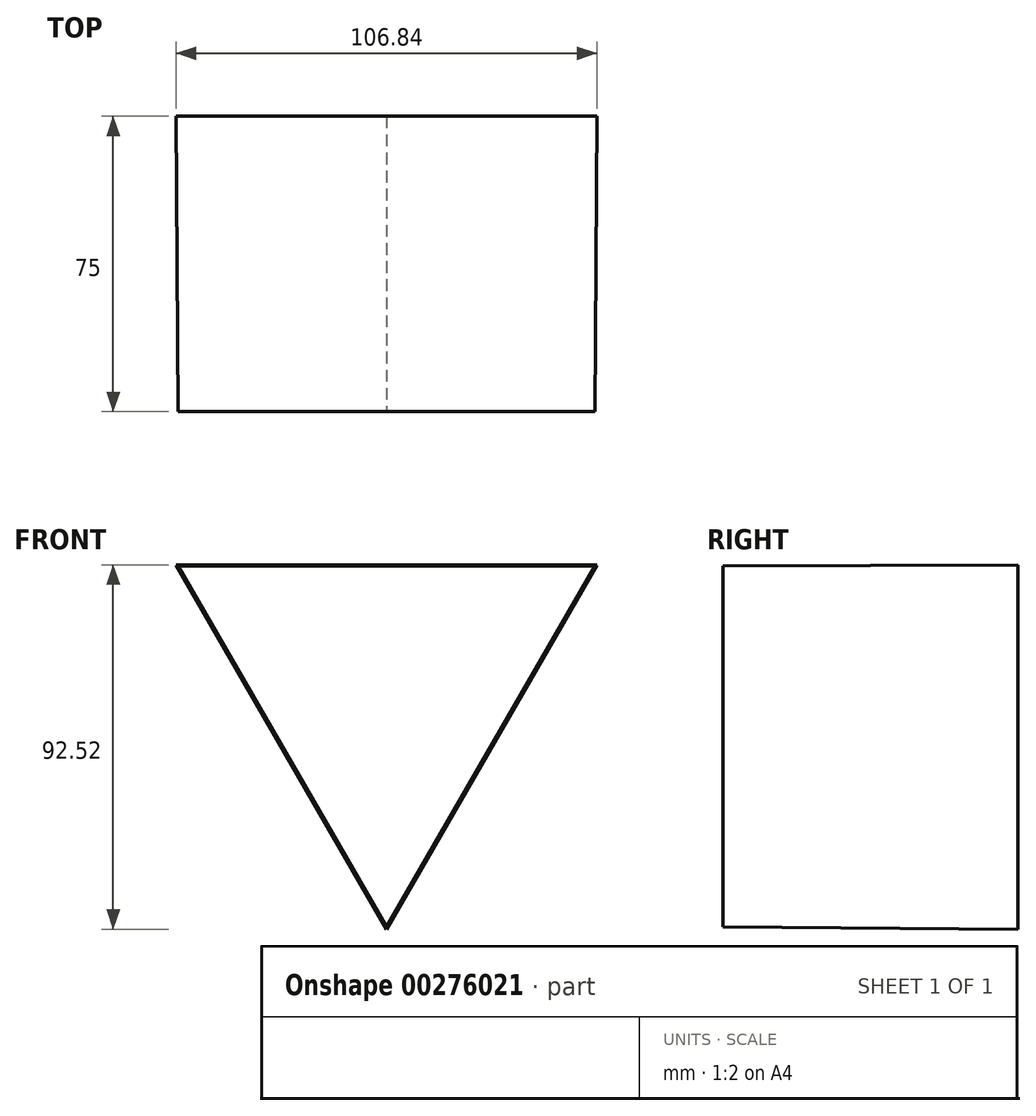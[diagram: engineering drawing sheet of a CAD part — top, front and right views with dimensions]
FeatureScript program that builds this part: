
annotation { "Feature Type Name" : "Feature", "Feature Type Description" : "" }
export const myFeature = defineFeature(function(context is Context, id is Id, definition is map)
    precondition{}
    {
        {
            var Q0;
            Q0=qCreatedBy(makeId("Front.planeOp"),FACE);
            var sketch = newSketch(context, id + "F0", { "sketchPlane" : qUnion([Q0])});
            skCircle(sketch, "E0.cCircle", {"center": v(0, 0) * mm, "radius": 30.84 * mm, "construction": true});
            skLineSegment(sketch, "E0.0", {"start": v(-53.42, 30.84) * mm, "end": v(53.42, 30.84) * mm});
            skLineSegment(sketch, "E0.1", {"start": v(53.42, 30.84) * mm, "end": v(0, -61.68) * mm});
            skLineSegment(sketch, "E0.2", {"start": v(0, -61.68) * mm, "end": v(-53.42, 30.84) * mm});
            skPoint(sketch, "E0.0.midPoint", {"position": v(0, 30.84) * mm});
            skSolve(sketch);
        }
        {
            var Q0;
            Q0=qCreatedBy(makeId("Front.planeOp"),FACE);
            cPlane(context, id + "F1", {"entities" : qUnion([Q0]), "cplaneType" : CPlaneType.OFFSET, "offset" : 75 * mm, "width" : 150 * mm, "height" : 150 * mm});
        }
        {
            var Q0;
            Q0=qCreatedBy(id+"F1.planeOp",FACE);
            var sketch = newSketch(context, id + "F2", { "sketchPlane" : qUnion([Q0])});
            skCircle(sketch, "E1.cCircle", {"center": v(0, 0) * mm, "radius": 30.55 * mm, "construction": true});
            skLineSegment(sketch, "E1.0", {"start": v(-52.92, 30.55) * mm, "end": v(52.92, 30.55) * mm});
            skLineSegment(sketch, "E1.1", {"start": v(52.92, 30.55) * mm, "end": v(0, -61.1) * mm});
            skLineSegment(sketch, "E1.2", {"start": v(0, -61.1) * mm, "end": v(-52.92, 30.55) * mm});
            skPoint(sketch, "E1.0.midPoint", {"position": v(0, 30.55) * mm});
            skSolve(sketch);
        }
        {
            var Q0;
            Q0=makeQuery(id+"F0.imprint","IMPRINT",FACE,{"disambiguationData":[TD([[makeQuery(id+"F0.imprint","IMPRINT",EDGE,{"derivedFrom":sQuery(id+"F0.wireOp",EDGE,"E0.0")}),-1.0]])]});
            var Q1;
            Q1=makeQuery(id+"F2.imprint","IMPRINT",FACE,{"disambiguationData":[TD([[makeQuery(id+"F2.imprint","IMPRINT",EDGE,{"derivedFrom":sQuery(id+"F2.wireOp",EDGE,"E1.0")}),-1.0]])]});
            loft(context, id + "F3", {"sheetProfilesArray" : [{ "sheetProfileEntities" : qUnion([Q0]) }, { "sheetProfileEntities" : qUnion([Q1]) }]});
        }
    });
